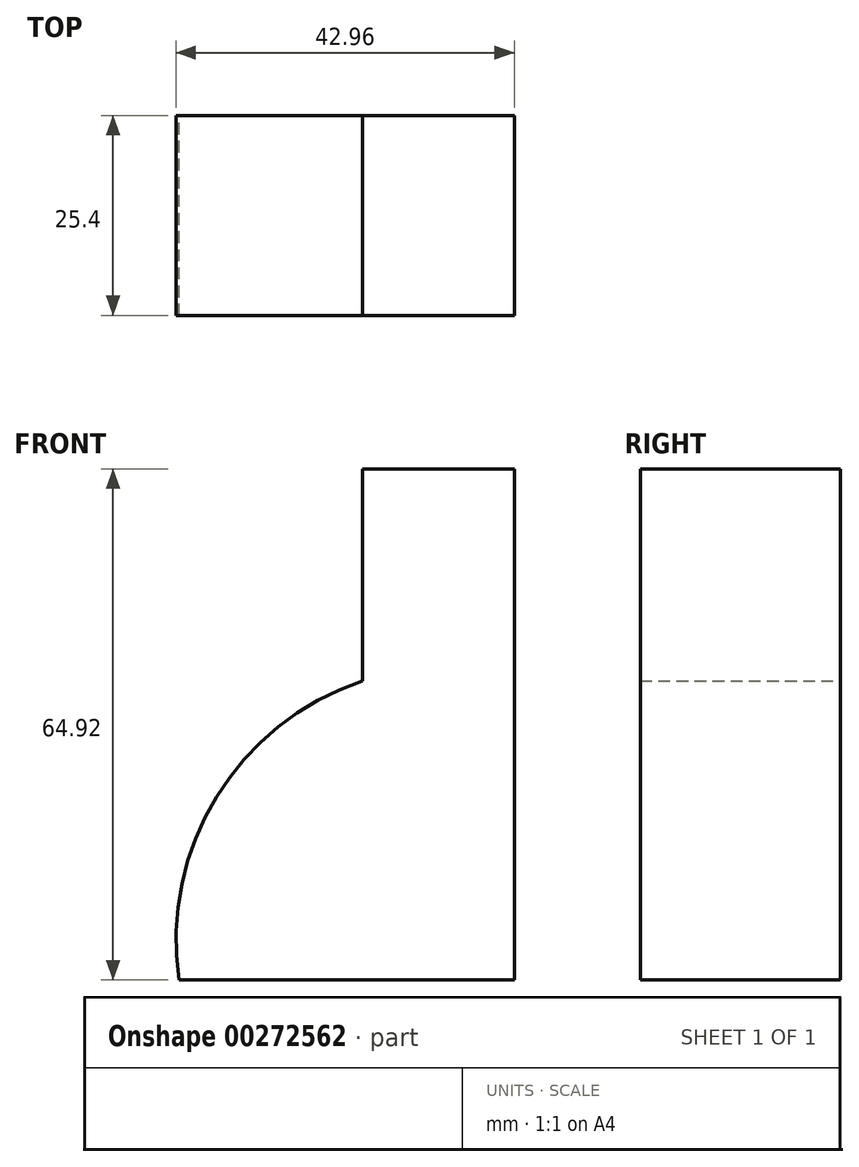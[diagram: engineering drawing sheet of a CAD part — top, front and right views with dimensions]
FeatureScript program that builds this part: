
annotation { "Feature Type Name" : "Feature", "Feature Type Description" : "" }
export const myFeature = defineFeature(function(context is Context, id is Id, definition is map)
    precondition{}
    {
        {
            var Q0;
            Q0=qCreatedBy(makeId("Front.planeOp"),FACE);
            var sketch = newSketch(context, id + "F0", { "sketchPlane" : qUnion([Q0])});
            skLineSegment(sketch, "E0", {"start": v(0, 0) * mm, "end": v(42.58, 0) * mm});
            skLineSegment(sketch, "E1", {"start": v(42.58, 0) * mm, "end": v(42.58, 64.92) * mm});
            skLineSegment(sketch, "E2", {"start": v(42.58, 64.92) * mm, "end": v(23.3, 64.92) * mm});
            skLineSegment(sketch, "E3", {"start": v(23.3, 64.92) * mm, "end": v(23.3, 38) * mm});
            skArc(sketch, "E4", {"start": v(23.3, 38) * mm, "mid": v(4.74, 23.24) * mm, "end": v(0, 0) * mm});
            skSolve(sketch);
        }
        {
            var Q0;
            Q0 = qSketchRegion(id + "F0", true);
            extrude(context, id + "F1", {"entities" : qUnion([Q0]), "depth" : 25.4 * mm});
        }
    });
